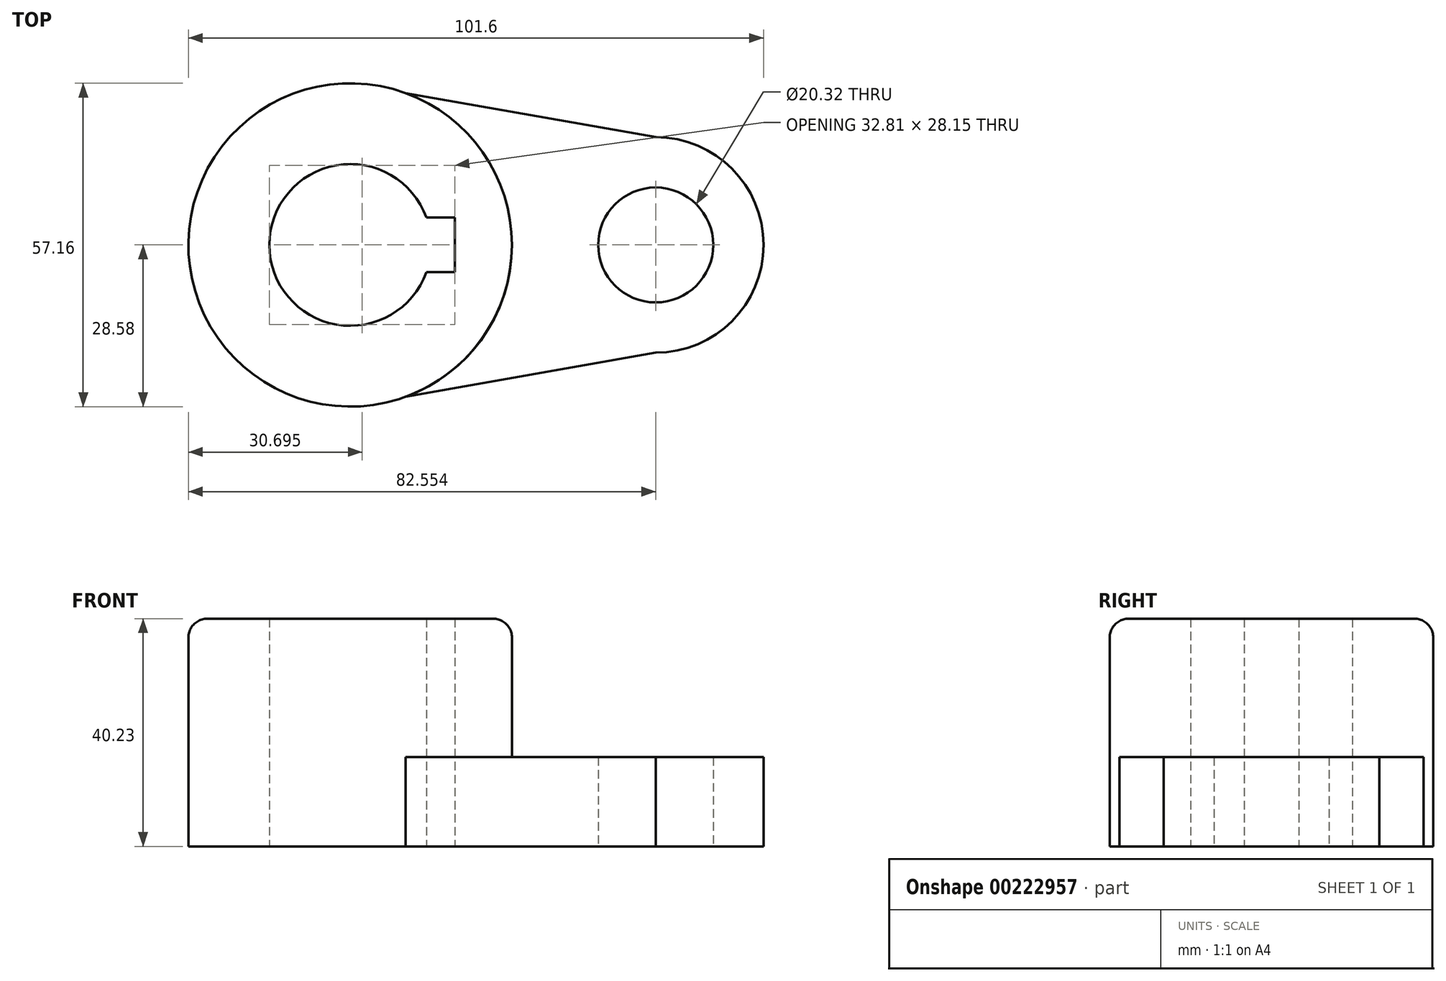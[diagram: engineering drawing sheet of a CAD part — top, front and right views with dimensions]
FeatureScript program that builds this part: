
annotation { "Feature Type Name" : "Feature", "Feature Type Description" : "" }
export const myFeature = defineFeature(function(context is Context, id is Id, definition is map)
    precondition{}
    {
        {
            var Q0;
            Q0=qCreatedBy(makeId("Top.planeOp"),FACE);
            var sketch = newSketch(context, id + "F0", { "sketchPlane" : qUnion([Q0])});
            skCircle(sketch, "E0", {"center": v(-39.66, 0) * mm, "radius": 28.57 * mm});
            skArc(sketch, "E1", {"start": v(-26.21, 4.83) * mm, "mid": v(-53.95, 0) * mm, "end": v(-26.21, -4.83) * mm});
            skLineSegment(sketch, "E2.bottom", {"start": v(-21.14, 4.83) * mm, "end": v(-26.21, 4.83) * mm});
            skLineSegment(sketch, "E2.top", {"start": v(-21.14, -4.83) * mm, "end": v(-26.21, -4.83) * mm});
            skLineSegment(sketch, "E2.left", {"start": v(-21.14, 4.83) * mm, "end": v(-21.14, -4.83) * mm});
            skLineSegment(sketch, "E3", {"start": v(-39.66, 0) * mm, "end": v(14.31, 0) * mm});
            skCircle(sketch, "E4", {"center": v(14.31, 0) * mm, "radius": 10.16 * mm});
            skArc(sketch, "E5", {"start": v(14.31, -19.05) * mm, "mid": v(33.36, 0) * mm, "end": v(14.31, 19.05) * mm});
            skLineSegment(sketch, "E6", {"start": v(14.31, 19.05) * mm, "end": v(-29.88, 26.85) * mm});
            skLineSegment(sketch, "E7", {"start": v(14.31, -19.05) * mm, "end": v(-29.88, -26.85) * mm});
            skSolve(sketch);
        }
        {
            var Q0;
            Q0=makeQuery(id+"F0.imprint","IMPRINT",FACE,{"disambiguationData":[TD([[makeQuery(id+"F0.imprint","IMPRINT",EDGE,{"derivedFrom":sQuery(id+"F0.wireOp",EDGE,"E1")}),-1.0]])]});
            extrude(context, id + "F1", {"entities" : qUnion([Q0]), "depth" : 40.23 * mm});
        }
        {
            var Q0;
            Q0 = qSketchRegion(id + "F0", true);
            extrude(context, id + "F2", {"entities" : qUnion([Q0]), "operationType" : NewBodyOperationType.ADD, "depth" : 15.77 * mm});
        }
        {
            var Q0;
            Q0=makeQuery(id+"F1.opExtrude","CAP_EDGE",EDGE,{"disambiguationData":[OSD([sQuery(id+"F0.wireOp",EDGE,"E0")])],"isStart":false});
            fillet(context, id + "F3", {"entities" : qUnion([Q0]), "radius" : 3.3 * mm, "tangentPropagation" : true, "allowEdgeOverflow" : false});
        }
    });
